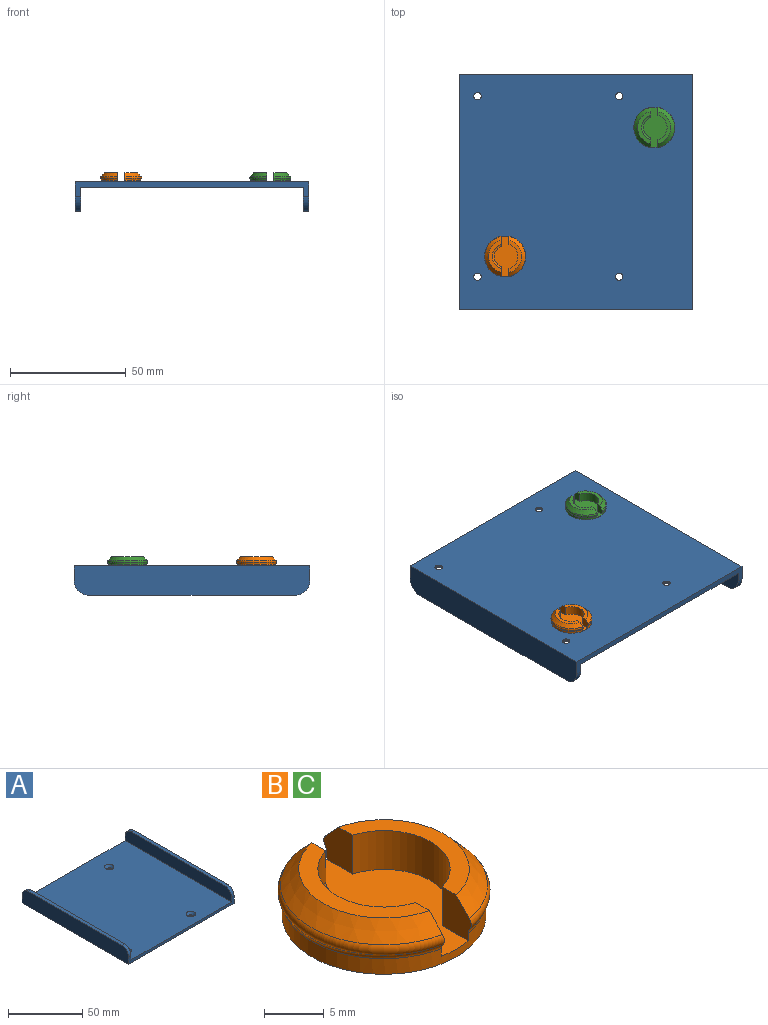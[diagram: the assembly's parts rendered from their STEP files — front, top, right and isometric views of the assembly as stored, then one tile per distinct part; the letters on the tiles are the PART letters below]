
ASSEMBLY  parts=3 mates=2
PART A: 26 faces, bbox 100.8x101.6x12.7 mm
  f0: plane 101.6x12.7mm, normal (-1,0,0), area 1273mm2, adj f1,f7,f8,f9,f11,f13
  f1: plane 101.6x100.81mm, normal (0,0,-1), area 9731.2mm2, adj f0,f2,f8,f9,f14,f16,f18,f20
  f2: plane 101.6x12.7mm, normal (1,0,0), area 1273mm2, adj f1,f3,f8,f9,f10,f12
  f3: plane 88.9x2.38mm, normal (0,0,1), area 211.7mm2, adj f2,f4,f10,f12
  f4: plane 101.6x10.32mm, normal (-1,0,0), area 1031.1mm2, adj f3,f5,f8,f9,f10,f12
  f5: plane 101.6x96.04mm, normal (0,0,1), area 9631.4mm2, adj f4,f6,f8,f9,f15,f17,f19,f21
  f6: plane 101.6x10.32mm, normal (1,0,0), area 1031.1mm2, adj f5,f7,f8,f9,f11,f13
  f7: plane 88.9x2.38mm, normal (0,0,1), area 211.7mm2, adj f0,f6,f11,f13
  f8: plane 100.81x6.35mm, normal (0,1,0), area 258.9mm2, adj f0,f1,f2,f4,f5,f6,f12,f13
  f9: plane 100.81x6.35mm, normal (0,-1,0), area 258.9mm2, adj f0,f1,f2,f4,f5,f6,f10,f11
  f10: cylinder r=6.35mm len=6.35mm, axis (-1,0,0), area 23.8mm2, adj f2,f3,f4,f9
  f11: cylinder r=6.35mm len=6.35mm, axis (-1,0,0), area 23.8mm2, adj f0,f6,f7,f9
  f12: cylinder r=6.35mm len=6.35mm, axis (1,0,0), area 23.8mm2, adj f2,f3,f4,f8
  f13: cylinder r=6.35mm len=6.35mm, axis (1,0,0), area 23.8mm2, adj f0,f6,f7,f8
  f14: cylinder r=1.59mm len=3.18mm, axis (0,0,1), area 5.5mm2, adj f1,f15
  f15: cone r=1.59mm half-angle=41deg, axis (0,0,1), area 36.2mm2, adj f5,f14
  f16: cylinder r=1.59mm len=3.18mm, axis (0,0,1), area 5.5mm2, adj f1,f17
  f17: cone r=1.59mm half-angle=41deg, axis (0,0,1), area 36.2mm2, adj f5,f16
  f18: cylinder r=1.59mm len=3.18mm, axis (0,0,1), area 5.5mm2, adj f1,f19
  f19: cone r=1.59mm half-angle=41deg, axis (0,0,1), area 36.2mm2, adj f5,f18
  f20: cylinder r=1.59mm len=3.18mm, axis (0,0,1), area 5.5mm2, adj f1,f21
  f21: cone r=1.59mm half-angle=41deg, axis (0,0,1), area 36.2mm2, adj f5,f20
  f22: cylinder r=8.73mm len=17.46mm, axis (0,0,-1), area 43.5mm2, adj f1,f23
  f23: plane 17.46x17.46mm, normal (0,0,-1), area 239.5mm2, adj f22
  f24: cylinder r=8.73mm len=17.46mm, axis (0,0,-1), area 43.5mm2, adj f1,f25
  f25: plane 17.46x17.46mm, normal (0,0,-1), area 239.5mm2, adj f24
PART B: 18 faces, bbox 19.3x19x4.9 mm
  f0: cylinder r=5.52mm len=10.58mm, axis (0,0,1), area 56.1mm2, adj f2,f7,f14,f17
  f1: plane 13.87x5.52mm, normal (0,0,1), area 26.4mm2, adj f9,f10,f15,f16
  f2: plane 13.87x5.52mm, normal (0,0,1), area 26.4mm2, adj f0,f3,f14,f17
  f3: cone r=8.64mm half-angle=42.6deg, axis (0,0,-1), area 48.5mm2, adj f2,f4,f14,f17
  f4: torus R=8.05mm, axis (0,0,1), area 27.3mm2, adj f3,f5,f14,f17
  f5: torus R=9.3mm, axis (0,0,1), area 12.5mm2, adj f4,f6,f14,f17
  f6: cylinder r=8.51mm len=17.02mm, axis (0,0,1), area 79.8mm2, adj f5,f7,f12,f13,f14,f15,f16,f17
  f7: plane 17.02x10.26mm, normal (0,0,1), area 104.8mm2, adj f0,f6,f8,f14,f15,f16,f17
  f8: torus R=4.73mm, axis (0,0,1), area 16.4mm2, adj f7,f9,f15,f16
  f9: cylinder r=5.52mm len=10.58mm, axis (0,0,1), area 44.9mm2, adj f1,f8,f15,f16
  f10: cone r=8.64mm half-angle=42.6deg, axis (0,0,-1), area 48.5mm2, adj f1,f11,f15,f16
  f11: torus R=8.05mm, axis (0,0,1), area 27.3mm2, adj f10,f12,f15,f16
  f12: torus R=9.3mm, axis (0,0,1), area 12.5mm2, adj f6,f11,f15,f16
  f13: plane 17.02x17.02mm, normal (0,0,-1), area 227.5mm2, adj f6
  f14: plane 4x3.44mm, normal (-1,0,0), area 11.4mm2, adj f0,f2,f3,f4,f5,f6,f7
  f15: plane 4.37x4.1mm, normal (1,0,0), area 11.6mm2, adj f1,f6,f7,f8,f9,f10,f11,f12
  f16: plane 4.37x4.1mm, normal (1,0,0), area 11.6mm2, adj f1,f6,f7,f8,f9,f10,f11,f12
  f17: plane 4x3.44mm, normal (-1,0,0), area 11.4mm2, adj f0,f2,f3,f4,f5,f6,f7
PART C: same geometry as B
PLACE A rot(axis=(1,0,0),180deg) t=(-24.34,-21.57,-9.87)mm
PLACE B t=(-54.89,-49.35,-9.48)mm
PLACE C t=(9.41,6.21,-9.48)mm
MATE pin_slot B.f0 <-> A.f24  axis (0,0,-1) through (-54.89,-49.35,-9.48)mm
MATE pin_slot C.f0 <-> A.f22  axis (0,0,-1) through (9.41,6.21,-9.48)mm
